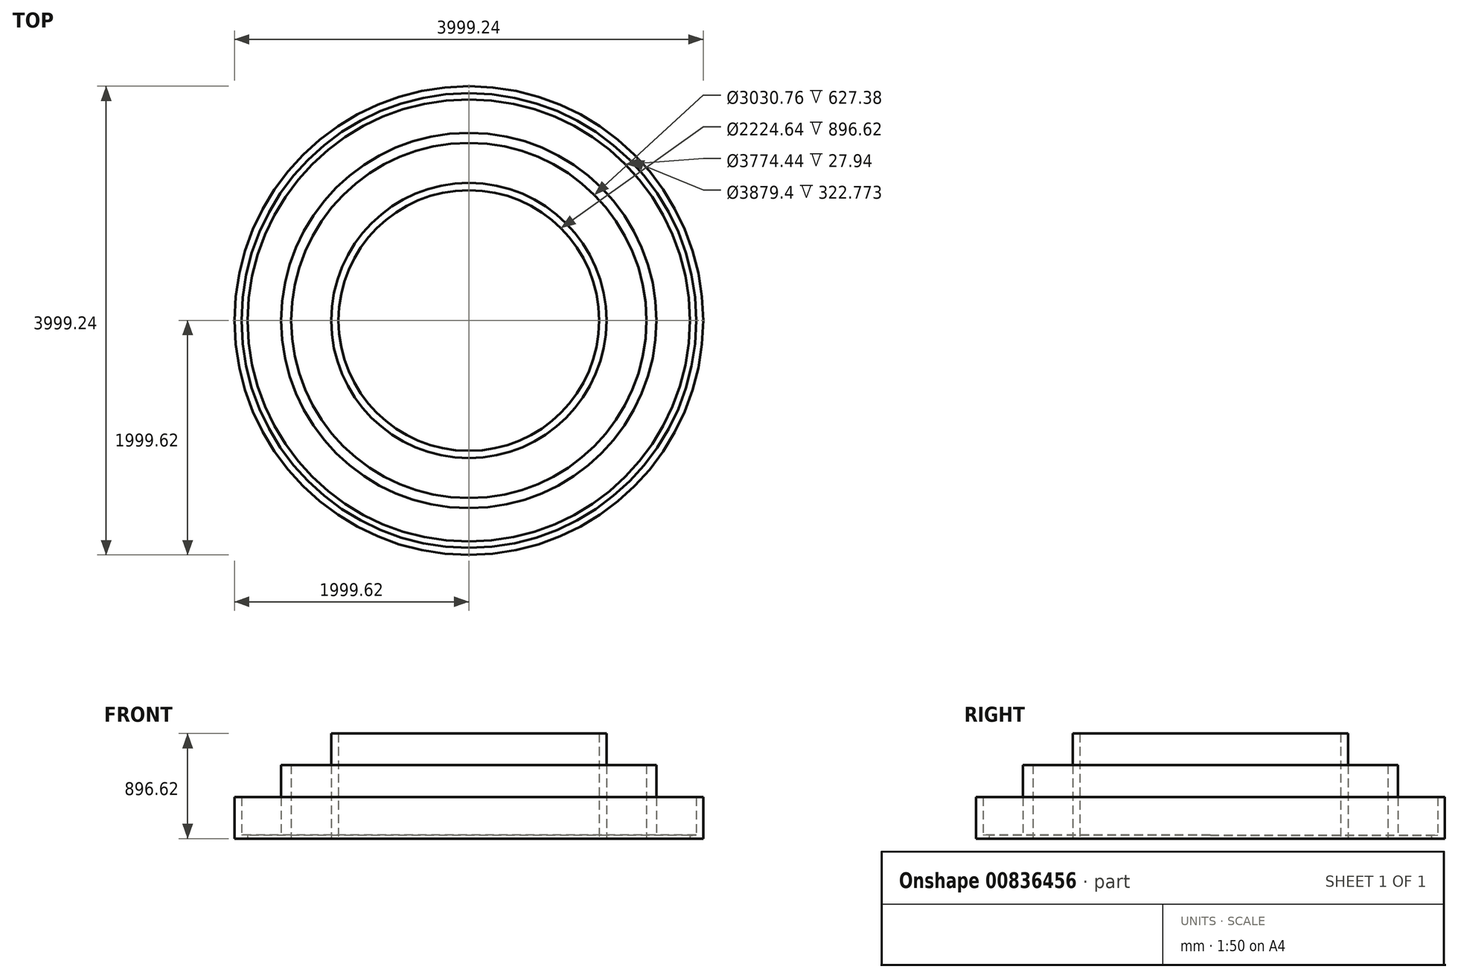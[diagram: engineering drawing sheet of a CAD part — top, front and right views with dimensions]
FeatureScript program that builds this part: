
annotation { "Feature Type Name" : "Feature", "Feature Type Description" : "" }
export const myFeature = defineFeature(function(context is Context, id is Id, definition is map)
    precondition{}
    {
        {
            var Q0;
            Q0=qCreatedBy(makeId("Front.planeOp"),FACE);
            var sketch = newSketch(context, id + "F0", { "sketchPlane" : qUnion([Q0])});
            skLineSegment(sketch, "E0", {"start": v(-523.57, -51.89) * mm, "end": v(-523.57, -23.95) * mm});
            skLineSegment(sketch, "E1", {"start": v(-523.57, -51.89) * mm, "end": v(1363.65, -51.89) * mm});
            skLineSegment(sketch, "E2", {"start": v(-523.57, -51.89) * mm, "end": v(-983.05, -51.89) * mm});
            skLineSegment(sketch, "E3", {"start": v(-584.53, -21.22) * mm, "end": v(-523.57, -23.95) * mm});
            skLineSegment(sketch, "E4", {"start": v(1363.65, -51.89) * mm, "end": v(1363.65, -25.56) * mm});
            skPoint(sketch, "E5.start.orphan", {"position": v(-983.05, 11.1) * mm});
            skLineSegment(sketch, "E6", {"start": v(-584.53, -21.22) * mm, "end": v(-584.53, -51.89) * mm});
            skSolve(sketch);
        }
        {
            var Q0;
            Q0=makeQuery(id+"F0.imprint","IMPRINT",FACE,{"disambiguationData":[TD([[makeQuery(id+"F0.imprint","IMPRINT",EDGE,{"derivedFrom":sQuery(id+"F0.wireOp",EDGE,"E0")}),1.0]])]});
            var Q1;
            Q1=sQuery(id+"F0.wireOp",EDGE,"E4");
            revolve(context, id + "F1", {"surfaceOperationType" : NewSurfaceOperationType.NEW, "entities" : qUnion([Q0]), "axis" : qUnion([Q1]), "revolveType" : RevolveType.FULL});
        }
        {
            var Q0;
            Q0=makeQuery(id+"F1.opRevolve","SWEPT_FACE",FACE,{"disambiguationData":[OSD([sQuery(id+"F0.wireOp",EDGE,"E2")])]});
            var sketch = newSketch(context, id + "F2", { "sketchPlane" : qUnion([Q0])});
            skCircle(sketch, "E7", {"center": v(1363.65, 0) * mm, "radius": 1939.7 * mm});
            skCircle(sketch, "E8", {"center": v(1363.65, 0) * mm, "radius": 1999.62 * mm});
            skCircle(sketch, "E9", {"center": v(1363.65, 0) * mm, "radius": 1112.32 * mm});
            skCircle(sketch, "E10", {"center": v(1363.65, 0) * mm, "radius": 1174 * mm});
            skCircle(sketch, "E11", {"center": v(1363.65, 0) * mm, "radius": 1515.38 * mm});
            skCircle(sketch, "E12", {"center": v(1363.65, 0) * mm, "radius": 1601.32 * mm});
            skSolve(sketch);
        }
        {
            var Q0;
            Q0=makeQuery(id+"F2.imprint","IMPRINT",FACE,{"disambiguationData":[TD([[makeQuery(id+"F2.imprint","IMPRINT",EDGE,{"derivedFrom":sQuery(id+"F2.wireOp",EDGE,"E11")}),-1.0]])]});
            extrude(context, id + "F3", {"entities" : qUnion([Q0]), "oppositeDirection" : true, "depth" : 627.38 * mm, "offsetDistance" : 25.4 * mm});
        }
        {
            var Q0;
            Q0=makeQuery(id+"F2.imprint","IMPRINT",FACE,{"disambiguationData":[TD([[makeQuery(id+"F2.imprint","IMPRINT",EDGE,{"derivedFrom":sQuery(id+"F2.wireOp",EDGE,"E9")}),-1.0]])]});
            extrude(context, id + "F4", {"entities" : qUnion([Q0]), "oppositeDirection" : true, "depth" : 896.62 * mm, "offsetDistance" : 25.4 * mm});
        }
        {
            var Q0;
            Q0=makeQuery(id+"F2.imprint","IMPRINT",FACE,{"disambiguationData":[TD([[makeQuery(id+"F2.imprint","IMPRINT",EDGE,{"derivedFrom":sQuery(id+"F2.wireOp",EDGE,"E7")}),-1.0]])]});
            extrude(context, id + "F5", {"entities" : qUnion([Q0]), "operationType" : NewBodyOperationType.ADD, "oppositeDirection" : true, "depth" : 353.06 * mm, "offsetDistance" : 25.4 * mm});
        }
        {
            var Q0;
            Q0=makeQuery(id+"F2.imprint","IMPRINT",FACE,{"disambiguationData":[TD([[makeQuery(id+"F2.imprint","IMPRINT",EDGE,{"derivedFrom":sQuery(id+"F2.wireOp",EDGE,"E8")}),1.0]])]});
            extrude(context, id + "F6", {"entities" : qUnion([Q0]), "operationType" : NewBodyOperationType.ADD, "oppositeDirection" : true, "depth" : 353.06 * mm, "offsetDistance" : 25.4 * mm});
        }
        {
            var Q0;
            Q0=qCreatedBy(makeId("Front.planeOp"),FACE);
            var sketch = newSketch(context, id + "F7", { "sketchPlane" : qUnion([Q0])});
            skCircle(sketch, "E13", {"center": v(1363.6, 0) * mm, "radius": 25.29 * mm});
            skLineSegment(sketch, "E14", {"start": v(1363.6, -26.1) * mm, "end": v(1363.6, -25.5) * mm});
            skSolve(sketch);
        }
        {
            var Q0;
            Q0=sQuery(id+"F7.wireOp",EDGE,"E13");
            extrude(context, id + "F8", {"bodyType" : ToolBodyType.SURFACE, "surfaceEntities" : qUnion([Q0]), "depth" : 1991.36 * mm, "offsetDistance" : 25.4 * mm});
        }
        {
            var Q0;
            Q0=sQuery(id+"F7.wireOp",EDGE,"E13");
            extrude(context, id + "F9", {"bodyType" : ToolBodyType.SURFACE, "surfaceOperationType" : NewSurfaceOperationType.ADD, "surfaceEntities" : qUnion([Q0]), "oppositeDirection" : true, "depth" : 1988.82 * mm, "offsetDistance" : 25.4 * mm});
        }
        {
            var Q0;
            Q0=qCreatedBy(makeId("Right.planeOp"),FACE);
            var sketch = newSketch(context, id + "F10", { "sketchPlane" : qUnion([Q0])});
            skCircle(sketch, "E15", {"center": v(0, 74.41) * mm, "radius": 37.16 * mm});
            skSolve(sketch);
        }
        {
            var Q0;
            Q0=sQuery(id+"F10.wireOp",EDGE,"E15");
            extrude(context, id + "F11", {"bodyType" : ToolBodyType.SURFACE, "surfaceEntities" : qUnion([Q0]), "depth" : 3307.08 * mm, "offsetDistance" : 25.4 * mm});
        }
        {
            var Q0;
            Q0=sQuery(id+"F10.wireOp",EDGE,"E15");
            extrude(context, id + "F12", {"bodyType" : ToolBodyType.SURFACE, "surfaceOperationType" : NewSurfaceOperationType.ADD, "surfaceEntities" : qUnion([Q0]), "oppositeDirection" : true, "depth" : 589.28 * mm, "offsetDistance" : 25.4 * mm});
        }
    });
